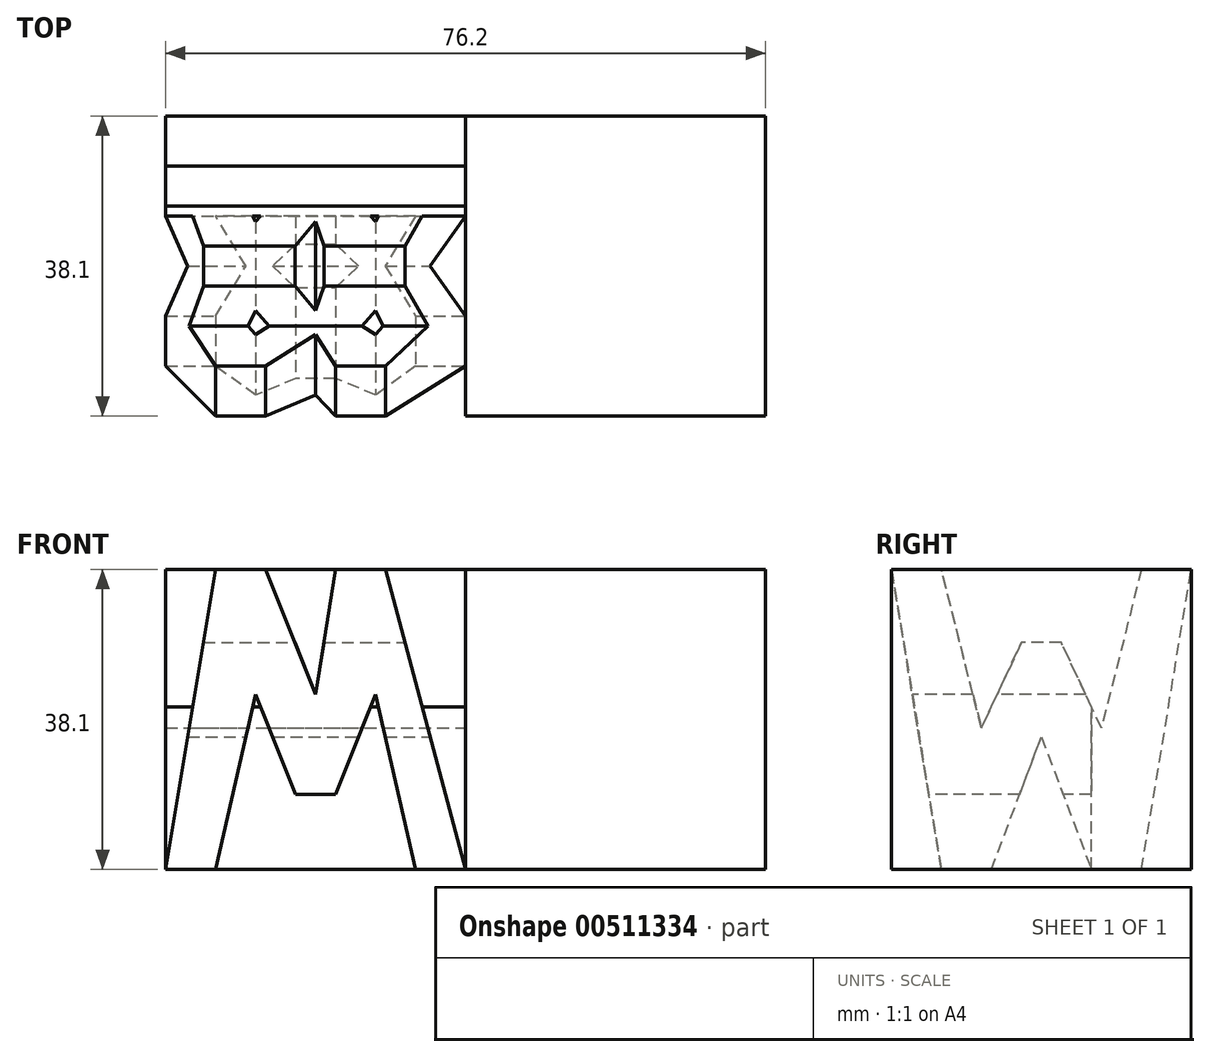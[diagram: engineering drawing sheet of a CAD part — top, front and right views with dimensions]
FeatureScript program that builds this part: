
annotation { "Feature Type Name" : "Feature", "Feature Type Description" : "" }
export const myFeature = defineFeature(function(context is Context, id is Id, definition is map)
    precondition{}
    {
        {
            var Q0;
            Q0=qCreatedBy(makeId("Front.planeOp"),FACE);
            cPlane(context, id + "F0", {"entities" : qUnion([Q0]), "cplaneType" : CPlaneType.OFFSET, "offset" : 38.1 * mm, "width" : 152.4 * mm, "height" : 152.4 * mm});
        }
        {
            var Q0;
            Q0=qCreatedBy(makeId("Right.planeOp"),FACE);
            cPlane(context, id + "F1", {"entities" : qUnion([Q0]), "cplaneType" : CPlaneType.OFFSET, "offset" : 38.1 * mm, "width" : 152.4 * mm, "height" : 152.4 * mm});
        }
        {
            var Q0;
            Q0=qCreatedBy(id+"F1.planeOp",FACE);
            var sketch = newSketch(context, id + "F2", { "sketchPlane" : qUnion([Q0])});
            skLineSegment(sketch, "E0", {"start": v(0, 0) * mm, "end": v(-38.1, 0) * mm});
            skLineSegment(sketch, "E1", {"start": v(-38.1, 0) * mm, "end": v(-38.1, 38.1) * mm});
            skLineSegment(sketch, "E2", {"start": v(-38.1, 38.1) * mm, "end": v(0, 38.1) * mm});
            skLineSegment(sketch, "E3", {"start": v(0, 38.1) * mm, "end": v(0, 0) * mm});
            skSolve(sketch);
        }
        {
            var Q0;
            Q0 = qSketchRegion(id + "F2", true);
            extrude(context, id + "F3", {"entities" : qUnion([Q0]), "depth" : 38.1 * mm, "offsetDistance" : 25.4 * mm});
        }
        {
            var Q0;
            Q0=qCreatedBy(id+"F1.planeOp",FACE);
            var sketch = newSketch(context, id + "F4", { "sketchPlane" : qUnion([Q0])});
            skLineSegment(sketch, "E4", {"start": v(-38.1, 38.1) * mm, "end": v(-31.75, 0) * mm});
            skLineSegment(sketch, "E5", {"start": v(-31.75, 0) * mm, "end": v(-25.4, 0) * mm});
            skLineSegment(sketch, "E6", {"start": v(-25.4, 0) * mm, "end": v(-19.05, 16.84) * mm});
            skLineSegment(sketch, "E7", {"start": v(-19.05, 16.84) * mm, "end": v(-12.7, 0) * mm});
            skLineSegment(sketch, "E8", {"start": v(-12.7, 0) * mm, "end": v(-6.35, 0) * mm});
            skLineSegment(sketch, "E9", {"start": v(-6.35, 0) * mm, "end": v(0, 38.1) * mm});
            skLineSegment(sketch, "E10", {"start": v(0, 38.1) * mm, "end": v(-6.35, 38.1) * mm});
            skLineSegment(sketch, "E11", {"start": v(-6.35, 38.1) * mm, "end": v(-11.43, 17.95) * mm});
            skLineSegment(sketch, "E12", {"start": v(-11.43, 17.95) * mm, "end": v(-16.5, 28.81) * mm});
            skLineSegment(sketch, "E13", {"start": v(-16.5, 28.81) * mm, "end": v(-21.59, 28.81) * mm});
            skLineSegment(sketch, "E14", {"start": v(-21.59, 28.81) * mm, "end": v(-26.67, 17.95) * mm});
            skLineSegment(sketch, "E15", {"start": v(-26.67, 17.95) * mm, "end": v(-31.75, 38.1) * mm});
            skLineSegment(sketch, "E16", {"start": v(-31.75, 38.1) * mm, "end": v(-38.1, 38.1) * mm});
            skLineSegment(sketch, "E17.bottom", {"start": v(0, 0) * mm, "end": v(-38.1, 0) * mm});
            skLineSegment(sketch, "E17.top", {"start": v(0, 38.1) * mm, "end": v(-38.1, 38.1) * mm});
            skLineSegment(sketch, "E17.left", {"start": v(0, 0) * mm, "end": v(0, 38.1) * mm});
            skLineSegment(sketch, "E17.right", {"start": v(-38.1, 0) * mm, "end": v(-38.1, 38.1) * mm});
            skSolve(sketch);
        }
        {
            var Q0;
            Q0 = qSketchRegion(id + "F2", true);
            extrude(context, id + "F5", {"entities" : qUnion([Q0]), "oppositeDirection" : true, "depth" : 38.1 * mm, "offsetDistance" : 25.4 * mm});
        }
        {
            var Q0;
            {var subQ0=sQuery(id+"F4.wireOp",EDGE,"E11");Q0=makeQuery(id+"F4.imprint","IMPRINT",FACE,{"disambiguationData":[TD([[makeQuery(id+"F4.imprint","IMPRINT",EDGE,{"derivedFrom":subQ0}),-1.0]])]});}
            var Q1;
            {var subQ0=sQuery(id+"F4.wireOp",EDGE,"E4");Q1=makeQuery(id+"F4.imprint","IMPRINT",FACE,{"disambiguationData":[TD([[makeQuery(id+"F4.imprint","IMPRINT",EDGE,{"derivedFrom":subQ0}),-1.0]])]});}
            var Q2;
            {var subQ0=sQuery(id+"F4.wireOp",EDGE,"E6");Q2=makeQuery(id+"F4.imprint","IMPRINT",FACE,{"disambiguationData":[TD([[makeQuery(id+"F4.imprint","IMPRINT",EDGE,{"derivedFrom":subQ0}),-1.0]])]});}
            var Q3;
            {var subQ0=sQuery(id+"F4.wireOp",EDGE,"E9");Q3=makeQuery(id+"F4.imprint","IMPRINT",FACE,{"disambiguationData":[TD([[makeQuery(id+"F4.imprint","IMPRINT",EDGE,{"derivedFrom":subQ0}),-1.0]])]});}
            extrude(context, id + "F6", {"entities" : qUnion([Q0, Q1, Q2, Q3]), "operationType" : NewBodyOperationType.REMOVE, "oppositeDirection" : true, "depth" : 38.1 * mm, "offsetDistance" : 25.4 * mm});
        }
        {
            var Q0;
            Q0=qCreatedBy(id+"F0.planeOp",FACE);
            var sketch = newSketch(context, id + "F7", { "sketchPlane" : qUnion([Q0])});
            skLineSegment(sketch, "E18.bottom", {"start": v(0, 0) * mm, "end": v(38.1, 0) * mm});
            skLineSegment(sketch, "E18.top", {"start": v(0, 38.1) * mm, "end": v(38.1, 38.1) * mm});
            skLineSegment(sketch, "E18.left", {"start": v(0, 0) * mm, "end": v(0, 38.1) * mm});
            skLineSegment(sketch, "E18.right", {"start": v(38.1, 0) * mm, "end": v(38.1, 38.1) * mm});
            skLineSegment(sketch, "E19", {"start": v(0, 0) * mm, "end": v(6.35, 38.1) * mm});
            skLineSegment(sketch, "E20", {"start": v(6.35, 38.1) * mm, "end": v(12.7, 38.1) * mm});
            skLineSegment(sketch, "E21", {"start": v(12.7, 38.1) * mm, "end": v(19.05, 22.22) * mm});
            skLineSegment(sketch, "E22", {"start": v(19.05, 22.23) * mm, "end": v(21.59, 38.1) * mm});
            skLineSegment(sketch, "E23", {"start": v(21.59, 38.1) * mm, "end": v(27.94, 38.1) * mm});
            skLineSegment(sketch, "E24", {"start": v(27.94, 38.1) * mm, "end": v(38.1, 0) * mm});
            skLineSegment(sketch, "E25", {"start": v(31.75, 0) * mm, "end": v(26.67, 22.23) * mm});
            skLineSegment(sketch, "E26", {"start": v(26.67, 22.23) * mm, "end": v(21.59, 9.52) * mm});
            skLineSegment(sketch, "E27", {"start": v(21.59, 9.53) * mm, "end": v(16.5, 9.53) * mm});
            skLineSegment(sketch, "E28", {"start": v(16.5, 9.53) * mm, "end": v(11.43, 22.23) * mm});
            skLineSegment(sketch, "E29", {"start": v(11.43, 22.23) * mm, "end": v(6.35, 0) * mm});
            skLineSegment(sketch, "E30", {"start": v(6.35, 0) * mm, "end": v(0, 0) * mm});
            skSolve(sketch);
        }
        {
            var Q0;
            {var subQ0=sQuery(id+"F7.wireOp",EDGE,"E18.left");Q0=makeQuery(id+"F7.imprint","IMPRINT",FACE,{"disambiguationData":[TD([[makeQuery(id+"F7.imprint","IMPRINT",EDGE,{"derivedFrom":subQ0}),-1.0]])]});}
            var Q1;
            {var subQ0=sQuery(id+"F7.wireOp",EDGE,"E21");Q1=makeQuery(id+"F7.imprint","IMPRINT",FACE,{"disambiguationData":[TD([[makeQuery(id+"F7.imprint","IMPRINT",EDGE,{"derivedFrom":subQ0}),1.0]])]});}
            var Q2;
            {var subQ0=sQuery(id+"F7.wireOp",EDGE,"E18.right");Q2=makeQuery(id+"F7.imprint","IMPRINT",FACE,{"disambiguationData":[TD([[makeQuery(id+"F7.imprint","IMPRINT",EDGE,{"derivedFrom":subQ0}),1.0]])]});}
            var Q3;
            {var subQ0=sQuery(id+"F7.wireOp",EDGE,"E25");Q3=makeQuery(id+"F7.imprint","IMPRINT",FACE,{"disambiguationData":[TD([[makeQuery(id+"F7.imprint","IMPRINT",EDGE,{"derivedFrom":subQ0}),1.0]])]});}
            extrude(context, id + "F8", {"entities" : qUnion([Q0, Q1, Q2, Q3]), "operationType" : NewBodyOperationType.REMOVE, "oppositeDirection" : true, "depth" : 25.4 * mm, "offsetDistance" : 25.4 * mm});
        }
    });
